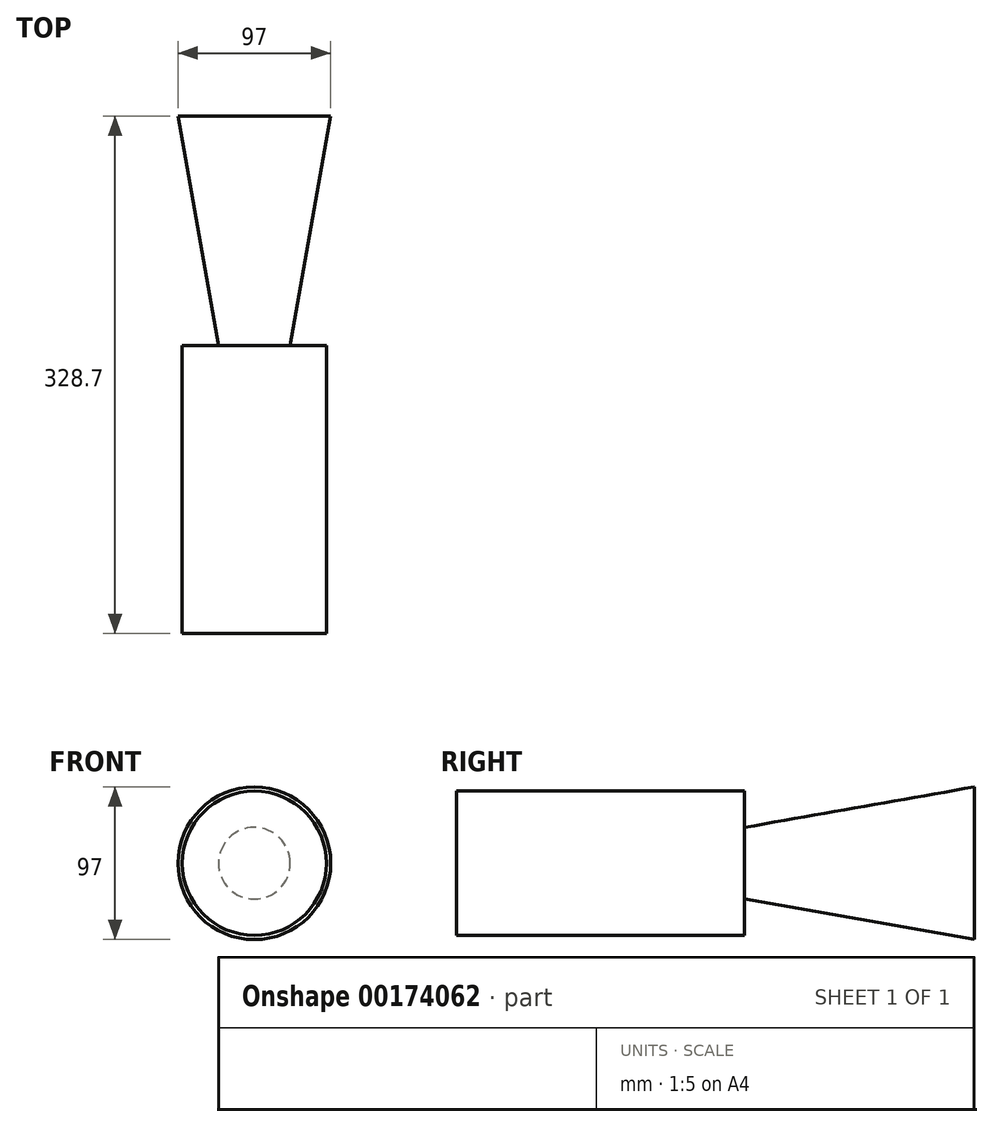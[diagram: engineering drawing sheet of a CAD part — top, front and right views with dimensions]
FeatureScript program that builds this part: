
annotation { "Feature Type Name" : "Feature", "Feature Type Description" : "" }
export const myFeature = defineFeature(function(context is Context, id is Id, definition is map)
    precondition{}
    {
        {
            var Q0;
            Q0=qCreatedBy(makeId("Front.planeOp"),FACE);
            var sketch = newSketch(context, id + "F0", { "sketchPlane" : qUnion([Q0])});
            skCircle(sketch, "E0", {"center": v(0, 0) * mm, "radius": 45.8 * mm});
            skSolve(sketch);
        }
        {
            var Q0;
            Q0 = qSketchRegion(id + "F0", true);
            extrude(context, id + "F1", {"entities" : qUnion([Q0]), "oppositeDirection" : true, "depth" : 182.7 * mm});
        }
        {
            var Q0;
            Q0=makeQuery(id+"F1.opExtrude","CAP_FACE",FACE,{"disambiguationData":[OSD([sQuery(id+"F0.wireOp",EDGE,"E0")])],"isStart":false});
            var sketch = newSketch(context, id + "F2", { "sketchPlane" : qUnion([Q0])});
            skCircle(sketch, "E1", {"center": v(0, 0) * mm, "radius": 22.75 * mm});
            skSolve(sketch);
        }
        {
            var Q0;
            Q0 = qSketchRegion(id + "F2", true);
            extrude(context, id + "F3", {"entities" : qUnion([Q0]), "operationType" : NewBodyOperationType.ADD, "depth" : 146 * mm, "hasDraft" : true, "draftAngle" : 10 * degree});
        }
    });
